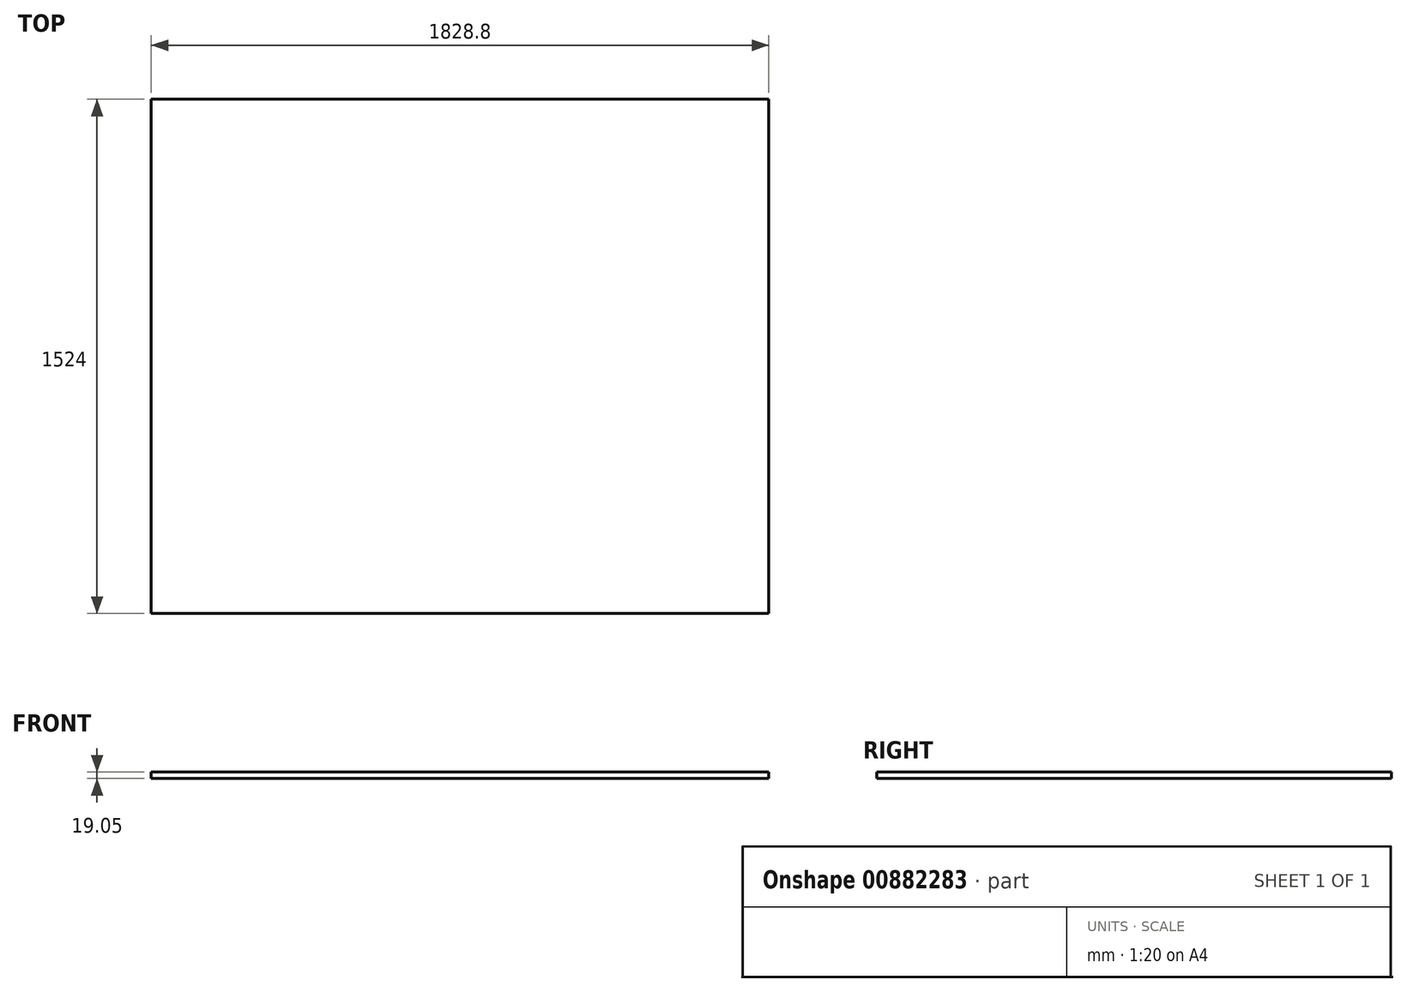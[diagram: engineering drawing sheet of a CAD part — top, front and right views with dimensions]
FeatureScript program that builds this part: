
annotation { "Feature Type Name" : "Feature", "Feature Type Description" : "" }
export const myFeature = defineFeature(function(context is Context, id is Id, definition is map)
    precondition{}
    {
        {
            var Q0;
            Q0=qCreatedBy(makeId("Top.planeOp"),FACE);
            var sketch = newSketch(context, id + "F0", { "sketchPlane" : qUnion([Q0])});
            skLineSegment(sketch, "E0.bottom", {"start": v(-914.4, -762) * mm, "end": v(914.4, -762) * mm});
            skLineSegment(sketch, "E0.top", {"start": v(-914.4, 762) * mm, "end": v(914.4, 762) * mm});
            skLineSegment(sketch, "E0.left", {"start": v(-914.4, -762) * mm, "end": v(-914.4, 762) * mm});
            skLineSegment(sketch, "E0.right", {"start": v(914.4, -762) * mm, "end": v(914.4, 762) * mm});
            skPoint(sketch, "E0.middle", {"position": v(0, 0) * mm});
            skSolve(sketch);
        }
        {
            var Q0;
            Q0=makeQuery(id+"F0.imprint","IMPRINT",FACE,{"disambiguationData":[TD([[makeQuery(id+"F0.imprint","IMPRINT",EDGE,{"derivedFrom":sQuery(id+"F0.wireOp",EDGE,"E0.bottom")}),1.0]])]});
            extrude(context, id + "F1", {"entities" : qUnion([Q0]), "depth" : 19.05 * mm, "offsetDistance" : 25.4 * mm});
        }
    });
